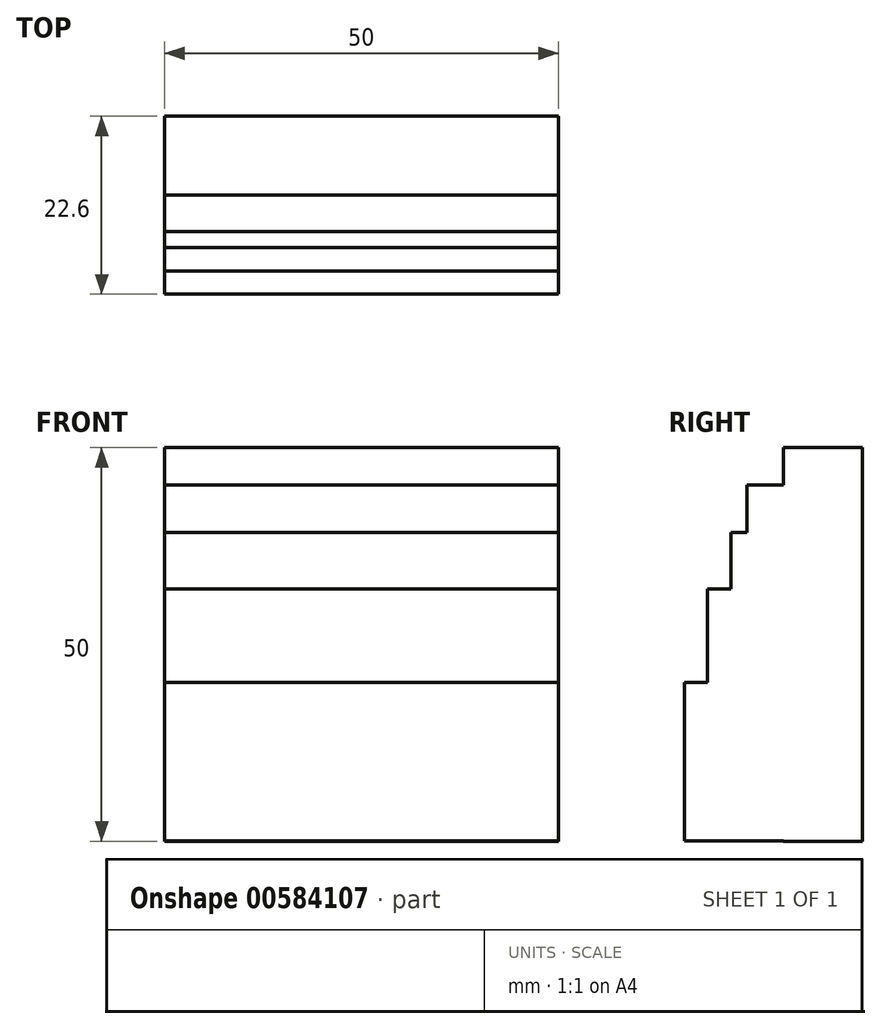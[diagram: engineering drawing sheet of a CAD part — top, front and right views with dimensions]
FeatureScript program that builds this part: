
annotation { "Feature Type Name" : "Feature", "Feature Type Description" : "" }
export const myFeature = defineFeature(function(context is Context, id is Id, definition is map)
    precondition{}
    {
        {
            var Q0;
            Q0=qCreatedBy(makeId("Front.planeOp"),FACE);
            var sketch = newSketch(context, id + "F0", { "sketchPlane" : qUnion([Q0])});
            skLineSegment(sketch, "E0.bottom", {"start": v(-25, 25) * mm, "end": v(25, 25) * mm});
            skLineSegment(sketch, "E0.top", {"start": v(-25, -25) * mm, "end": v(25, -25) * mm});
            skLineSegment(sketch, "E0.left", {"start": v(-25, 25) * mm, "end": v(-25, -25) * mm});
            skLineSegment(sketch, "E0.right", {"start": v(25, 25) * mm, "end": v(25, -25) * mm});
            skPoint(sketch, "E0.middle", {"position": v(0, 0) * mm});
            skSolve(sketch);
        }
        {
            var Q0;
            Q0=makeQuery(id+"F0.imprint","IMPRINT",FACE,{"disambiguationData":[TD([[makeQuery(id+"F0.imprint","IMPRINT",EDGE,{"derivedFrom":sQuery(id+"F0.wireOp",EDGE,"E0.bottom")}),-1.0]])]});
            extrude(context, id + "F1", {"entities" : qUnion([Q0]), "endBound" : BoundingType.SYMMETRIC, "depth" : 10 * mm, "offsetDistance" : 25.4 * mm});
        }
        {
            var Q0;
            Q0=qCreatedBy(makeId("Right.planeOp"),FACE);
            var sketch = newSketch(context, id + "F2", { "sketchPlane" : qUnion([Q0])});
            skLineSegment(sketch, "E1", {"start": v(-4.81, 20.27) * mm, "end": v(-9.62, 20.27) * mm});
            skLineSegment(sketch, "E2", {"start": v(-9.62, 20.27) * mm, "end": v(-9.62, 14.23) * mm});
            skLineSegment(sketch, "E3", {"start": v(-9.62, 14.23) * mm, "end": v(-11.67, 14.23) * mm});
            skLineSegment(sketch, "E4", {"start": v(-11.67, 14.23) * mm, "end": v(-11.67, 7.07) * mm});
            skLineSegment(sketch, "E5", {"start": v(-11.67, 7.07) * mm, "end": v(-14.64, 7.07) * mm});
            skLineSegment(sketch, "E6", {"start": v(-14.64, 7.07) * mm, "end": v(-14.64, -4.8) * mm});
            skLineSegment(sketch, "E7", {"start": v(-14.64, -4.8) * mm, "end": v(-17.6, -4.8) * mm});
            skLineSegment(sketch, "E8", {"start": v(-17.6, -4.8) * mm, "end": v(-17.6, -24.95) * mm});
            skLineSegment(sketch, "E9", {"start": v(-17.6, -24.95) * mm, "end": v(-4.81, -24.95) * mm});
            skLineSegment(sketch, "E10", {"start": v(-4.81, 22.24) * mm, "end": v(-4.81, -30.28) * mm, "construction": true});
            skPoint(sketch, "E10.startSnap0", {"position": v(-4.81, 20.27) * mm});
            skPoint(sketch, "E11.end.orphan", {"position": v(0, 20.27) * mm});
            skPoint(sketch, "E12.orphan", {"position": v(0, -24.95) * mm});
            skLineSegment(sketch, "E13", {"start": v(-4.81, 20.27) * mm, "end": v(-4.81, -24.95) * mm});
            skSolve(sketch);
        }
        {
            var Q0;
            Q0 = qSketchRegion(id + "F2", true);
            extrude(context, id + "F3", {"entities" : qUnion([Q0]), "operationType" : NewBodyOperationType.ADD, "endBound" : BoundingType.SYMMETRIC, "depth" : 50 * mm, "offsetDistance" : 25.4 * mm});
        }
    });
